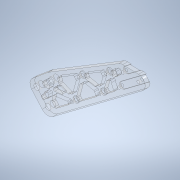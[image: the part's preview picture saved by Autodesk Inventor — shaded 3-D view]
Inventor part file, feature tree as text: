
AUTODESK INVENTOR PART (.ipt)
format: ipt  version: 2020.2 (Build 242310000, 310)  size: 803,840 bytes
history: native  units: mm
features: sketch x15, extrude x10, other x7, projected_geometry x7, fillet x3, hole x2
ambient origin geometry x8: Origin, YZ Plane, XZ Plane, XY Plane, X Axis, Y Axis, Z Axis, Center Point
bodies: Body1 (feature_tree)
feature tree (44):
  other  "ソリッド1"
  extrude  "押し出し1"  Depth=5.0mm TaperAngle=0.0deg
  sketch  "スケッチ2"
  extrude  "押し出し2"  Depth=1.0mm TaperAngle=0.0deg
  extrude  "押し出し3"  Depth=1.0mm TaperAngle=0.0deg
  extrude  "押し出し4"  Depth=1.0mm TaperAngle=0.0deg
  extrude  "押し出し5"  Depth=6.0mm
  hole  "穴1"  [1 undecoded]
  extrude  "押し出し6"  Depth=1.0mm TaperAngle=0.0deg
  sketch  "スケッチ7"
  sketch  "スケッチ8"
  hole  "穴2"  [1 undecoded]
  extrude  "押し出し7"  Depth=6.0mm
  extrude  "押し出し10"  Depth=6.0mm
  sketch  "スケッチ12"
  extrude  "押し出し11"  Depth=6.0mm
  fillet  "フィレット2"  Radius=6.0mm
  fillet  "フィレット3"  Radius=1.0mm
  sketch  "スケッチ14"
  extrude  "押し出し12"  Depth=9.0mm
  fillet  "フィレット4"  Radius=9.0mm
  sketch  "スケッチ16"
  sketch  "スケッチ1"
  sketch  "スケッチ3"
  projected_geometry  "投影ループ1"
  projected_geometry  "投影ループ2"
  sketch  "スケッチ4"
  sketch  "スケッチ5"
  sketch  "スケッチ6"
  projected_geometry  "投影ループ3"
  projected_geometry  "投影ループ4"
  projected_geometry  "投影ループ5"
  sketch  "スケッチ9"
  sketch  "スケッチ10"
  sketch  "スケッチ13"
  sketch  "スケッチ15"
  projected_geometry  "投影ループ6"
  projected_geometry  "投影ループ7"
  other  "断面エッジを投影1"
  other  "断面エッジを投影2"
  other  "断面エッジを投影4"
  other  "断面エッジを投影5"
  other  "断面エッジを投影6"
  other  "断面エッジを投影7"
note: 2 required parameter values undecoded (feature->parameter linkage not recoverable at this tier; creation-order binding heuristic only, values carry confidence <= 0.55)
